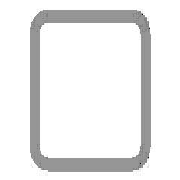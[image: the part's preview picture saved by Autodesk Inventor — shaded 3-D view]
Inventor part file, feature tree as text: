
AUTODESK INVENTOR PART (.ipt)
format: ipt  version: 2022.1 (Build 261234000, 234)  size: 134,656 bytes
history: native  units: mm (DEFAULTED — no unit token found)
features: other x4, sketch x3, extrude x1, plane x1
ambient origin geometry x8: Origin, YZ Plane, XZ Plane, XY Plane, X Axis, Y Axis, Z Axis, Center Point
bodies: Solid1 (feature_tree)
feature tree (9):
  parser-record x1  (decoder bookkeeping rows leaked as tree rows — omitted from the tree; the rows remain in map.json)
  other  "Driven Length"
  other  "Plano inicial"
  other  "Plano final"
  extrude  "Cuerpo"  TaperAngle=0.0deg  [1 undecoded]
  sketch  "Boceto"  dims[d10=40.0mm d11=40.0mm d12=5.0mm d13=-0.0mm d14=300.0mm d15=20.0mm d16=20.0mm d17=90.0deg d18=300.0mm]
  sketch  "Sketch3"  dims[d3=300.0mm d4=0.0mm]
  plane  "Work Plane3"
  sketch  "Sketch4"  dims[d7=7.5mm]
note: 1 required parameter value undecoded (feature->parameter linkage not recoverable at this tier; creation-order binding heuristic only, values carry confidence <= 0.55)
